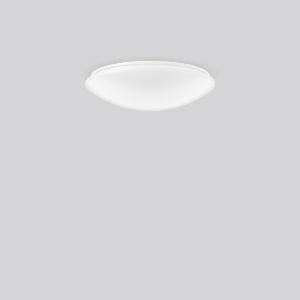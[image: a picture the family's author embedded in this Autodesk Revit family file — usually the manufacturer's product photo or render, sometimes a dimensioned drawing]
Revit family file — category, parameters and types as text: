
# Revit family: flat_polymero_311946_002_4_beda
name_source: partatom
category: Lighting Fixtures
units: mm (PartAtom-declared; Revit-internal decimal feet)

## family parameters
Cut with Voids When Loaded = No
Host = Face
Light Source = No
Part Type = Normal
Room Calculation Point = No
Round Connector Dimension = Use Diameter
Shared = No

## types (1)
- FLAT POLYMERO (1 x LED Modul 840, 2000 lm, 4000)
    Apparent Load = 19 VA
    CIE Flux Codes = 43 72 90 89 100
    Color Rendering = 80
    Color Temperature = 4000
    Default Elevation = 1800 mm
    Description = Series: FLAT POLYMERO
Decorative round surface-mounted luminaire. Base: metal, powder-coated. Diffuser made of plastic (polycarbonate), opal, shockproof. Diffuser fastening: patented push system. Suitable for Ceiling mounting, Wall (surface). 
Colour: white
Diameter: 360 mm
Height: 100 mm
Lamp: LED exchangeable
Socket: without socket
Colour temperature: 4000K
Colour rendering index (CRI): 83
System power: 19 W
Rated luminous flux: 2000 lm
Beam angle Down: 115°
Luminous efficiency: 105 lm/W
Control gear: AC Strom, dim.Ph.an-/abschnitt
Protection class: I
Type of protection: IP 40
    Height = 100 mm  [stored 0.328084 ft]
    Lamp = 1 x LED Modul 840
    Lamp Light Flux = 2000 lm
    Lamp count = 1
    Length = 360 mm
    Lifetime = 50000 h
    Luminous efficacy = 105 lm/W
    Manufacturer = RZB
    ModVariant = No
    Model = 311946.002.4
    Mounting Place = Ceiling, Wall
    Mounting Type = Surface mounted
    Number of Poles = 1
    OnlyDefault = Yes
    Power Factor = 1
    Product Name = FLAT POLYMERO
    Product group = Surface mounted ceiling and wall luminaires
    ProductGroupID = 305
    Protection Class = Protection class I
    Protection Degree = IP 40
    RLX_Detail_Level = 1
    RLX_Emergency_Light_Flux = 0 lm
    RLX_Emergency_Type = 0
    RLX_Emergency_Type_DB = No
    RlxData = <blob elided: 76565 chars, md5=daa0208d>
    Socket = socket
    Standby Power = 0 W
    System Light Flux = 2000 lm
    System Power = 19 W
    Type Comments = ALEA SPOT
    Type Image = 311523.002.1.jpg
    URL = http://relux.com
    VarID = ---
    Voltage = 230 V
    Voltage Range = 220-240 V
    Weight = 0.00 kg
    Width = 0 mm  [stored 0 ft]

note: [stored X ft] marks values corroborated as IEEE doubles in the binary element streams (Revit-internal decimal feet)

## geometry (parser evidence)
native form markers: Blend x4, Sweep x14
no freeform markers — native parametric forms only
